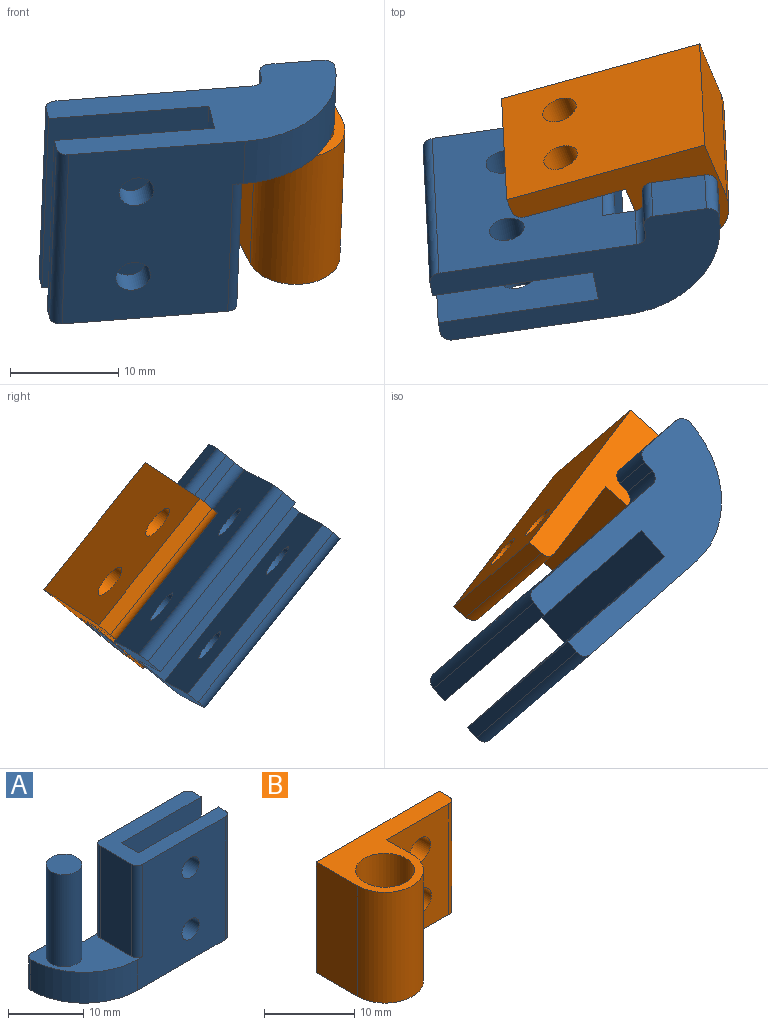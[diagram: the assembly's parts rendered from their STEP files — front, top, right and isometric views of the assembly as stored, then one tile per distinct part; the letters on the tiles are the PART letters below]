
ASSEMBLY  parts=2 mates=1
PART A: 27 faces, bbox 27.5x11x20 mm
  f0: plane 15x6mm, normal (-1,0,0), area 90mm2, adj f8,f12,f18,f21
  f1: plane 20x16.5mm, normal (0,-1,0), area 298.4mm2, adj f8,f9,f12,f18,f19,f24,f25,f26
  f2: plane 20x1.25mm, normal (1,0,0), area 25mm2, adj f3,f8,f9,f19
  f3: plane 20x15mm, normal (0,1,0), area 283.4mm2, adj f2,f4,f8,f9,f24,f25
  f4: plane 20x3.25mm, normal (1,0,0), area 65mm2, adj f3,f5,f8,f9
  f5: plane 20x15mm, normal (0,-1,0), area 283.4mm2, adj f4,f6,f8,f9,f22,f23
  f6: plane 20x1.5mm, normal (1,0,0), area 30mm2, adj f5,f8,f9,f20
  f7: plane 20x18.5mm, normal (0,1,0), area 308.4mm2, adj f8,f9,f12,f15,f20,f21,f22,f23
  f8: plane 17.5x8mm, normal (0,0,1), area 90.4mm2, adj f0,f1,f2,f3,f4,f5,f6,f7
  f9: plane 27.5x11mm, normal (0,0,-1), area 170.1mm2, adj f1,f2,f3,f4,f5,f6,f7,f10
  f10: plane 5x1mm, normal (1,0,0), area 5mm2, adj f9,f12,f15,f16
  f11: plane 5x5mm, normal (0,1,0), area 25mm2, adj f9,f12,f16,f17
  f12: plane 11x11mm, normal (0,0,1), area 62mm2, adj f0,f1,f7,f10,f11,f13,f15,f16
  f13: cylinder r=2.38mm len=15mm, axis (0,0,-1), area 223.8mm2, adj f12,f14
  f14: plane 4.75x4.75mm, normal (0,0,1), area 17.7mm2, adj f13
  f15: cylinder r=1mm len=5mm, axis (0,0,1), area 7.9mm2, adj f7,f9,f10,f12
  f16: cylinder r=1mm len=5mm, axis (0,0,-1), area 7.9mm2, adj f9,f10,f11,f12
  f17: cylinder r=1mm len=5mm, axis (0,0,-1), area 7.9mm2, adj f9,f11,f12,f26
  f18: cylinder r=1mm len=15mm, axis (0,0,-1), area 23.6mm2, adj f0,f1,f8,f12
  f19: cylinder r=1mm len=20mm, axis (0,0,-1), area 31.4mm2, adj f1,f2,f8,f9
  f20: cylinder r=1mm len=20mm, axis (0,0,-1), area 31.4mm2, adj f6,f7,f8,f9
  f21: cylinder r=1mm len=15mm, axis (0,0,-1), area 23.6mm2, adj f0,f7,f8,f12
  f22: cylinder r=1.62mm len=3.25mm, axis (0,-1,0), area 25.5mm2, adj f5,f7
  f23: cylinder r=1.62mm len=3.25mm, axis (0,-1,0), area 25.5mm2, adj f5,f7
  f24: cylinder r=1.62mm len=3.25mm, axis (0,-1,0), area 23mm2, adj f1,f3
  f25: cylinder r=1.62mm len=3.25mm, axis (0,-1,0), area 23mm2, adj f1,f3
  f26: cylinder r=10mm len=10mm, axis (0,0,-1), area 78.5mm2, adj f1,f9,f12,f17
PART B: 12 faces, bbox 19.3x10.8x15 mm
  f0: plane 15x1.5mm, normal (1,0,0), area 22.5mm2, adj f1,f7,f8,f11
  f1: plane 19.25x15mm, normal (0,1,0), area 272.2mm2, adj f0,f2,f7,f8,f9,f10
  f2: plane 15x6.5mm, normal (-1,0,0), area 97.5mm2, adj f1,f3,f7,f8
  f3: cylinder r=4.25mm len=15mm, axis (0,0,-1), area 200.3mm2, adj f2,f4,f7,f8
  f4: plane 15x4mm, normal (1,0,0), area 60mm2, adj f3,f6,f7,f8
  f5: cylinder r=3.25mm len=15mm, axis (0,0,-1), area 306.3mm2, adj f7,f8
  f6: plane 15x9.75mm, normal (0,-1,0), area 129.7mm2, adj f4,f7,f8,f9,f10,f11
  f7: plane 19.25x10.75mm, normal (0,0,1), area 77.1mm2, adj f0,f1,f2,f3,f4,f5,f6,f11
  f8: plane 19.25x10.75mm, normal (0,0,-1), area 77.1mm2, adj f0,f1,f2,f3,f4,f5,f6,f11
  f9: cylinder r=1.62mm len=3.25mm, axis (0,-1,0), area 25.5mm2, adj f1,f6
  f10: cylinder r=1.62mm len=3.25mm, axis (0,-1,0), area 25.5mm2, adj f1,f6
  f11: cylinder r=1mm len=15mm, axis (0,0,1), area 23.6mm2, adj f0,f6,f7,f8
PLACE A rot(axis=(-0.08,0.94,0.33),178.7deg) t=(-11.12,-29.12,26.74)mm
PLACE B rot(axis=(-0.15,0.93,0.33),175.7deg) t=(4.33,-20.95,26.25)mm
MATE revolute B.f3 <-> A.f13  axis (0.03,-0.62,0.78) through (3.86,-11.59,14.54)mm
